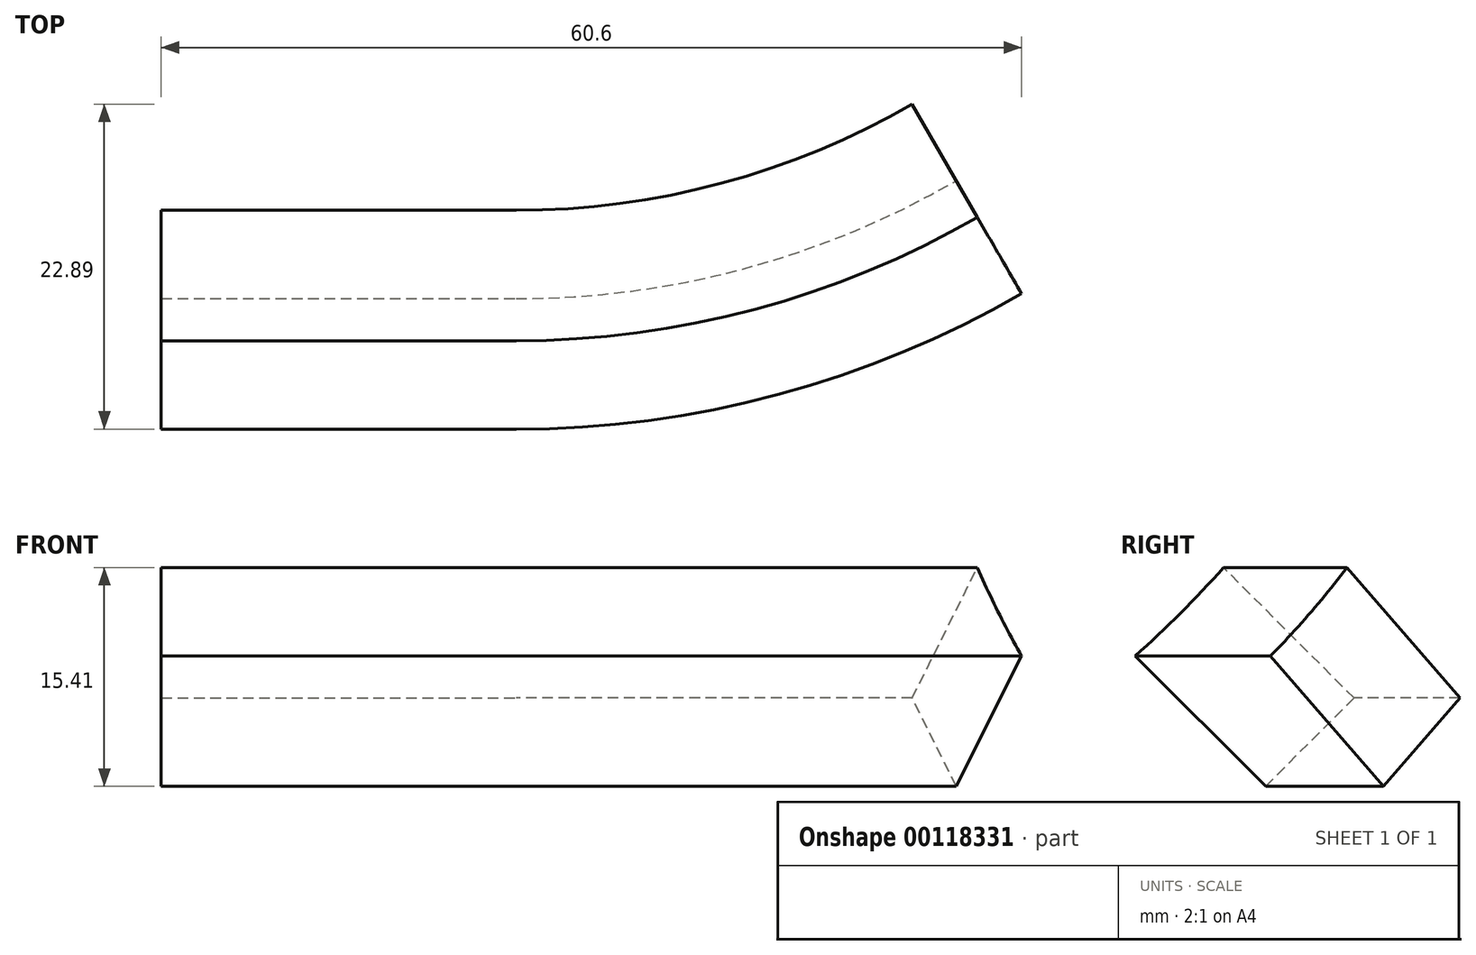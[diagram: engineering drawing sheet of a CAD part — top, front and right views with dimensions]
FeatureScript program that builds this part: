
annotation { "Feature Type Name" : "Feature", "Feature Type Description" : "" }
export const myFeature = defineFeature(function(context is Context, id is Id, definition is map)
    precondition{}
    {
        {
            var Q0;
            Q0=qCreatedBy(makeId("Top.planeOp"),FACE);
            var sketch = newSketch(context, id + "F0", { "sketchPlane" : qUnion([Q0])});
            skCircle(sketch, "E0", {"center": v(0, 0) * mm, "radius": 100 * mm});
            skCircle(sketch, "E1", {"center": v(0, 0) * mm, "radius": 50 * mm});
            skSolve(sketch);
        }
        {
            var Q0;
            Q0=qCreatedBy(makeId("Right.planeOp"),FACE);
            var sketch = newSketch(context, id + "F1", { "sketchPlane" : qUnion([Q0])});
            skPoint(sketch, "E2", {"position": v(0, 0) * mm});
            skLineSegment(sketch, "E3", {"start": v(0, 0) * mm, "end": v(0, 0) * mm});
            skLineSegment(sketch, "E4", {"start": v(0, 0) * mm, "end": v(-100, 0) * mm});
            skLineSegment(sketch, "E5", {"start": v(0, 0) * mm, "end": v(-50, 0) * mm});
            skLineSegment(sketch, "E6", {"start": v(-50, 0) * mm, "end": v(-50, 50) * mm});
            skArc(sketch, "E7", {"start": v(-100, 0) * mm, "mid": v(-67.99, 17.99) * mm, "end": v(-50, 50) * mm});
            skPoint(sketch, "E8", {"position": v(-67.99, 17.99) * mm});
            skLineSegment(sketch, "E9", {"start": v(-67.99, 17.99) * mm, "end": v(-58.9, 8.9) * mm});
            skLineSegment(sketch, "E10", {"start": v(-58.9, 8.9) * mm, "end": v(-55.79, 12) * mm});
            skLineSegment(sketch, "E11", {"start": v(-55.79, 12) * mm, "end": v(-64.98, 21.2) * mm});
            skLineSegment(sketch, "E12", {"start": v(-67.99, 17.99) * mm, "end": v(-64.98, 21.2) * mm});
            skLineSegment(sketch, "E13.MirrorCS", {"start": v(-62, 5.79) * mm, "end": v(-71.2, 14.98) * mm});
            skLineSegment(sketch, "E14.MirrorCS", {"start": v(-67.99, 17.99) * mm, "end": v(-71.2, 14.98) * mm});
            skLineSegment(sketch, "E15.MirrorCS", {"start": v(-58.9, 8.9) * mm, "end": v(-62, 5.79) * mm});
            skLineSegment(sketch, "E16", {"start": v(0, 0) * mm, "end": v(0, 24.15) * mm});
            skSolve(sketch);
        }
        {
            var Q0;
            {var subQ1=sQuery(id+"F1.wireOp",EDGE,"E9");Q0=makeQuery(id+"F1.imprint","IMPRINT",FACE,{"disambiguationData":[TD([[makeQuery(id+"F1.imprint","IMPRINT",EDGE,{"derivedFrom":subQ1}),1.0]])]});}
            var Q1;
            {var subQ1=sQuery(id+"F1.wireOp",EDGE,"E9");Q1=makeQuery(id+"F1.imprint","IMPRINT",FACE,{"disambiguationData":[TD([[makeQuery(id+"F1.imprint","IMPRINT",EDGE,{"derivedFrom":subQ1}),-1.0]])]});}
            var Q2;
            Q2=sQuery(id+"F1.wireOp",EDGE,"E16");
            revolve(context, id + "F2", {"entities" : qUnion([Q0, Q1]), "axis" : qUnion([Q2]), "revolveType" : RevolveType.ONE_DIRECTION, "angle" : 30 * degree});
        }
        {
            var Q0;
            {var subQ1=sQuery(id+"F1.wireOp",EDGE,"E9");Q0=makeQuery(id+"F1.imprint","IMPRINT",FACE,{"disambiguationData":[TD([[makeQuery(id+"F1.imprint","IMPRINT",EDGE,{"derivedFrom":subQ1}),-1.0]])]});}
            var Q1;
            {var subQ1=sQuery(id+"F1.wireOp",EDGE,"E9");Q1=makeQuery(id+"F1.imprint","IMPRINT",FACE,{"disambiguationData":[TD([[makeQuery(id+"F1.imprint","IMPRINT",EDGE,{"derivedFrom":subQ1}),1.0]])]});}
            extrude(context, id + "F3", {"entities" : qUnion([Q0, Q1]), "operationType" : NewBodyOperationType.ADD, "oppositeDirection" : true, "depth" : 25 * mm});
        }
    });
